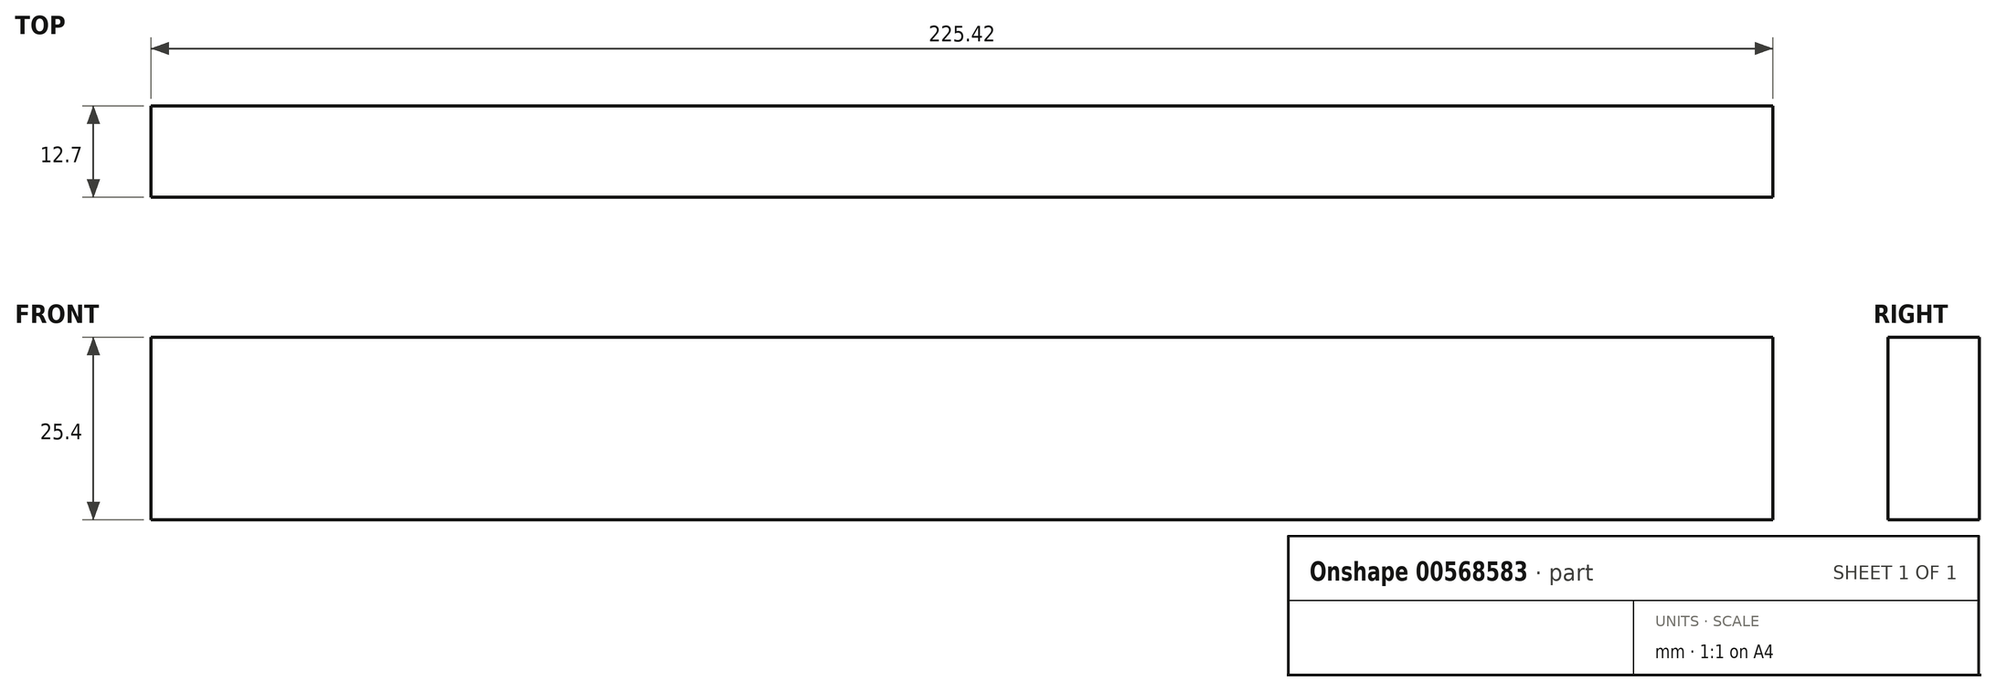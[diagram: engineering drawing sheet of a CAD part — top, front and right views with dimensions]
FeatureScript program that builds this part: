
annotation { "Feature Type Name" : "Feature", "Feature Type Description" : "" }
export const myFeature = defineFeature(function(context is Context, id is Id, definition is map)
    precondition{}
    {
        {
            var Q0;
            Q0=qCreatedBy(makeId("Right.planeOp"),FACE);
            var sketch = newSketch(context, id + "F0", { "sketchPlane" : qUnion([Q0])});
            skLineSegment(sketch, "E0.bottom", {"start": v(6.35, 12.7) * mm, "end": v(-6.35, 12.7) * mm});
            skLineSegment(sketch, "E0.top", {"start": v(6.35, -12.7) * mm, "end": v(-6.35, -12.7) * mm});
            skLineSegment(sketch, "E0.left", {"start": v(6.35, 12.7) * mm, "end": v(6.35, -12.7) * mm});
            skLineSegment(sketch, "E0.right", {"start": v(-6.35, 12.7) * mm, "end": v(-6.35, -12.7) * mm});
            skPoint(sketch, "E0.middle", {"position": v(0, 0) * mm});
            skSolve(sketch);
        }
        {
            var Q0;
            Q0 = qSketchRegion(id + "F0", true);
            extrude(context, id + "F1", {"entities" : qUnion([Q0]), "depth" : 225.42 * mm, "offsetDistance" : 25.4 * mm});
        }
    });
